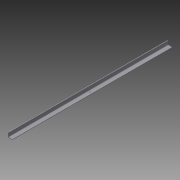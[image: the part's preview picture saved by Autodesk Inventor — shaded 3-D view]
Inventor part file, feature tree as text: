
AUTODESK INVENTOR PART (.ipt)
format: ipt  version: 2014 (Build 180170000, 170)  size: 86,528 bytes
history: native  units: in
note: dims shown in document units (in); Inventor stores cm internally (conversion verified against a paired STEP export)
features: sketch x2, extrude x1, hole x1
ambient origin geometry x8: Origin, YZ Plane, XZ Plane, XY Plane, X Axis, Y Axis, Z Axis, Center Point
bodies: Solid1 (feature_tree)
feature tree (4):
  extrude  "Extrusion1"  Depth=1.0in
  hole  "Hole1"  [1 undecoded]
  sketch  "Sketch1"  dims[d0=1.0in d1=1.0in]
  sketch  "Sketch3"  dims[d2=0.1181in d3=0.1476in d4=36.2362in d5=0.0in d10=0.25in d11=0.5in d12=0.25in d13=0.75in d14=0.375in d15=0.25in d16=0.5635in d17=1.0in d18=0.8108in]
note: 1 required parameter value undecoded (feature->parameter linkage not recoverable at this tier; creation-order binding heuristic only, values carry confidence <= 0.55)
